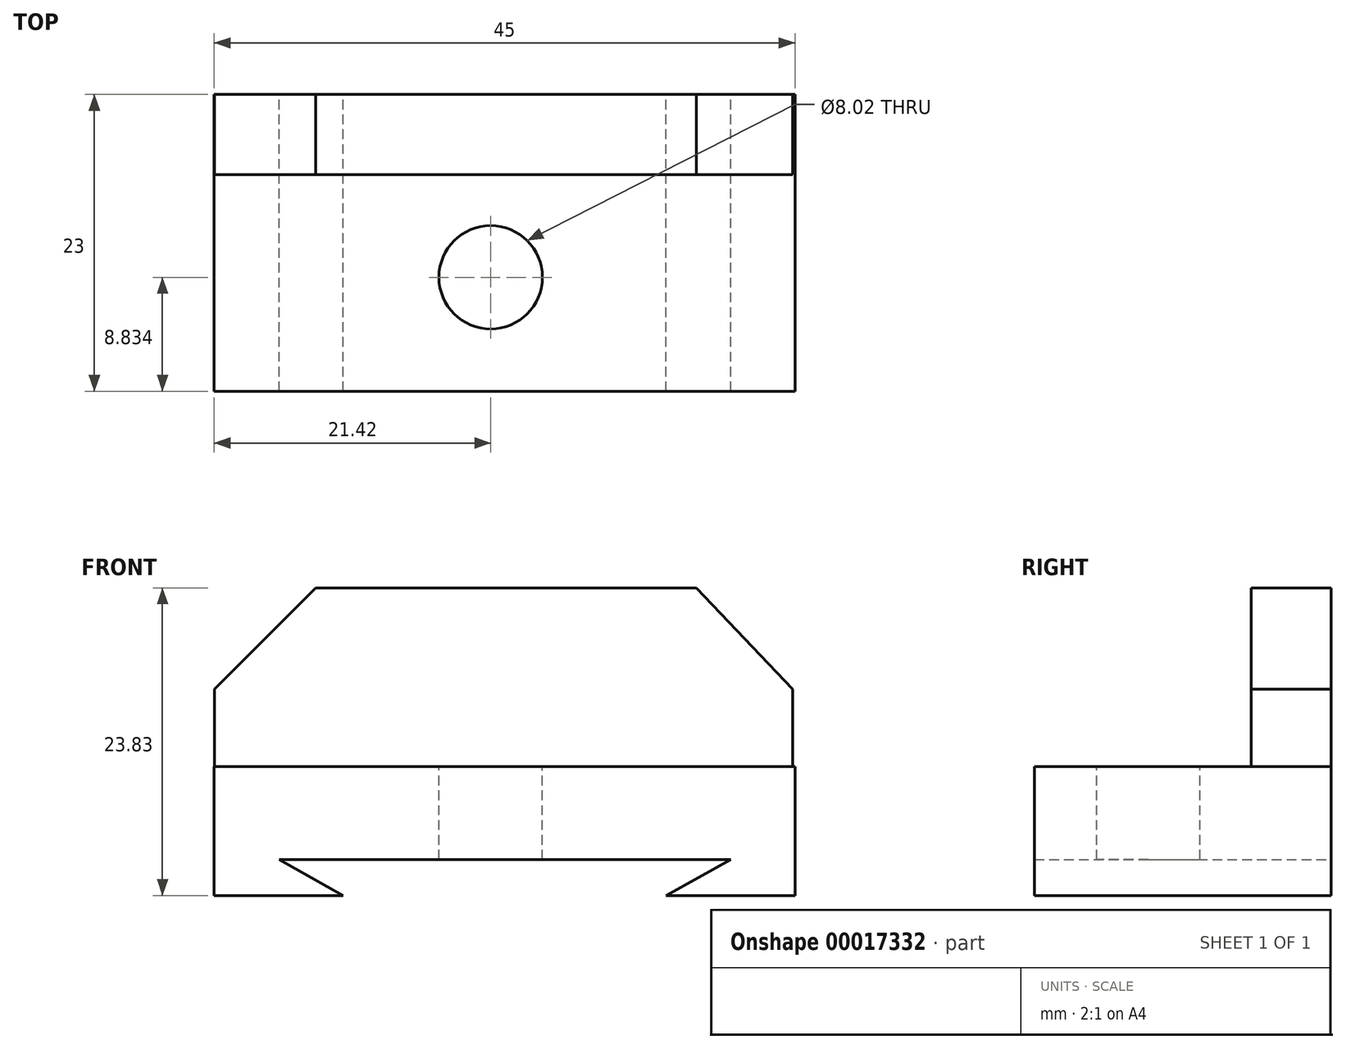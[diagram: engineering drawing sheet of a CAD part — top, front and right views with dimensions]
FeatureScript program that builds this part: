
annotation { "Feature Type Name" : "Feature", "Feature Type Description" : "" }
export const myFeature = defineFeature(function(context is Context, id is Id, definition is map)
    precondition{}
    {
        {
            var Q0;
            Q0=qCreatedBy(makeId("Front.planeOp"),FACE);
            var sketch = newSketch(context, id + "F0", { "sketchPlane" : qUnion([Q0])});
            skLineSegment(sketch, "E0", {"start": v(-15.26, -10) * mm, "end": v(-15.26, 0) * mm});
            skLineSegment(sketch, "E1", {"start": v(-15.26, 0) * mm, "end": v(29.74, 0) * mm});
            skLineSegment(sketch, "E2", {"start": v(29.74, 0) * mm, "end": v(29.74, -10) * mm});
            skLineSegment(sketch, "E3", {"start": v(29.74, -10) * mm, "end": v(19.74, -10) * mm});
            skLineSegment(sketch, "E4", {"start": v(19.74, -10) * mm, "end": v(24.78, -7.21) * mm});
            skLineSegment(sketch, "E5", {"start": v(24.78, -7.21) * mm, "end": v(-10.22, -7.21) * mm});
            skLineSegment(sketch, "E6", {"start": v(-10.22, -7.21) * mm, "end": v(-5.26, -10) * mm});
            skLineSegment(sketch, "E7", {"start": v(-5.26, -10) * mm, "end": v(-15.26, -10) * mm});
            skSolve(sketch);
        }
        {
            var Q0;
            Q0 = qSketchRegion(id + "F0", true);
            extrude(context, id + "F1", {"entities" : qUnion([Q0]), "depth" : 23 * mm});
        }
        {
            var Q0;
            Q0=qCreatedBy(makeId("Front.planeOp"),FACE);
            var sketch = newSketch(context, id + "F2", { "sketchPlane" : qUnion([Q0])});
            skLineSegment(sketch, "E8.bottom", {"start": v(-15.24, 0) * mm, "end": v(29.55, 0) * mm});
            skLineSegment(sketch, "E9", {"start": v(-7.4, 13.83) * mm, "end": v(-15.24, 5.99) * mm});
            skLineSegment(sketch, "E10", {"start": v(29.55, 5.99) * mm, "end": v(22.1, 13.83) * mm});
            skLineSegment(sketch, "E11", {"start": v(-15.24, 0) * mm, "end": v(-15.24, 5.99) * mm});
            skLineSegment(sketch, "E12", {"start": v(-7.4, 13.83) * mm, "end": v(22.1, 13.83) * mm});
            skLineSegment(sketch, "E13", {"start": v(29.55, 5.99) * mm, "end": v(29.55, 0) * mm});
            skSolve(sketch);
        }
        {
            var Q0;
            Q0=makeQuery(id+"F2.imprint","IMPRINT",FACE,{"disambiguationData":[TD([[makeQuery(id+"F2.imprint","IMPRINT",EDGE,{"derivedFrom":sQuery(id+"F2.wireOp",EDGE,"E8.bottom")}),1.0]])]});
            extrude(context, id + "F3", {"entities" : qUnion([Q0]), "operationType" : NewBodyOperationType.ADD, "depth" : 6.2 * mm});
        }
        {
            var Q0;
            Q0=makeQuery(id+"F1.opExtrude","SWEPT_FACE",FACE,{"disambiguationData":[OSD([sQuery(id+"F0.wireOp",EDGE,"E1")])]});
            var sketch = newSketch(context, id + "F4", { "sketchPlane" : qUnion([Q0])});
            skCircle(sketch, "E14", {"center": v(6.16, -14.17) * mm, "radius": 4 * mm});
            skSolve(sketch);
        }
        {
            var Q0;
            Q0=makeQuery(id+"F4.imprint","IMPRINT",FACE,{"disambiguationData":[TD([[makeQuery(id+"F4.imprint","IMPRINT",EDGE,{"derivedFrom":sQuery(id+"F4.wireOp",EDGE,"E14")}),1.0]])]});
            extrude(context, id + "F5", {"entities" : qUnion([Q0]), "operationType" : NewBodyOperationType.REMOVE, "oppositeDirection" : true, "depth" : 25 * mm});
        }
    });
